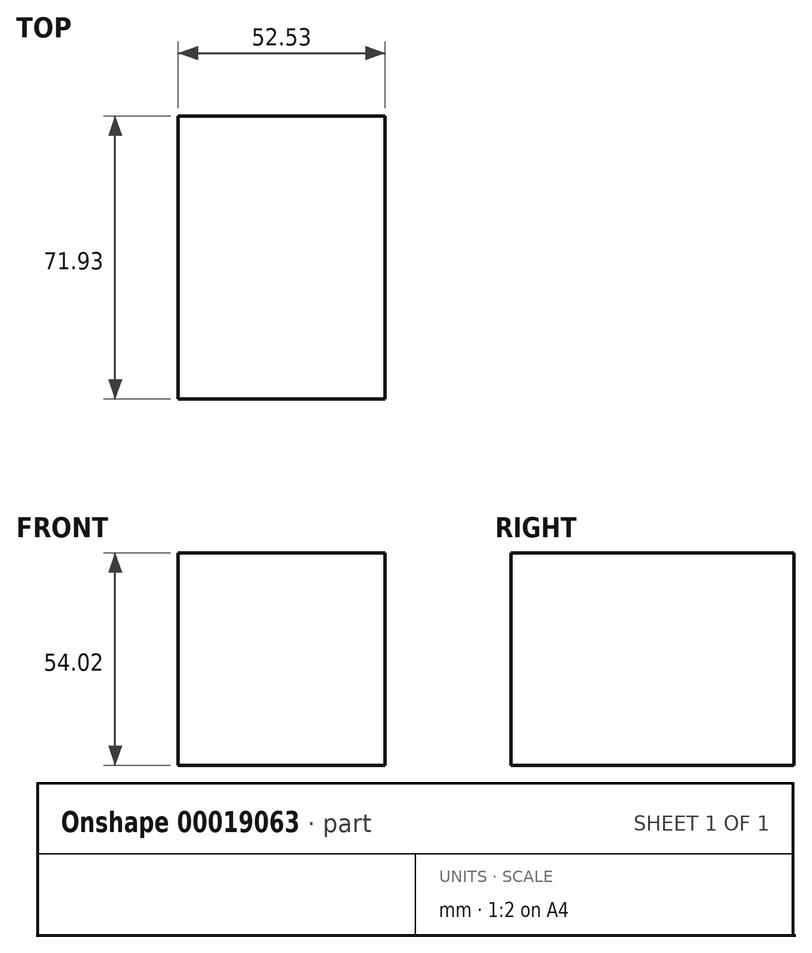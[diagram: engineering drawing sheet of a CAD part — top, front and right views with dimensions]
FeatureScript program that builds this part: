
annotation { "Feature Type Name" : "Feature", "Feature Type Description" : "" }
export const myFeature = defineFeature(function(context is Context, id is Id, definition is map)
    precondition{}
    {
        {
            var Q0;
            Q0=qCreatedBy(makeId("Front.planeOp"),FACE);
            var sketch = newSketch(context, id + "F0", { "sketchPlane" : qUnion([Q0])});
            skLineSegment(sketch, "E0.bottom", {"start": v(0, 0) * mm, "end": v(-52.53, 0) * mm});
            skLineSegment(sketch, "E0.top", {"start": v(0, 54.02) * mm, "end": v(-52.53, 54.02) * mm});
            skLineSegment(sketch, "E0.left", {"start": v(0, 0) * mm, "end": v(0, 54.02) * mm});
            skLineSegment(sketch, "E0.right", {"start": v(-52.53, 0) * mm, "end": v(-52.53, 54.02) * mm});
            skSolve(sketch);
        }
        {
            var Q0;
            Q0 = qSketchRegion(id + "F0", true);
            extrude(context, id + "F1", {"entities" : qUnion([Q0]), "oppositeDirection" : true, "depth" : 71.93 * mm});
        }
        {
            var Q0;
            Q0=makeQuery(id+"F1.opExtrude","SWEPT_FACE",FACE,{"disambiguationData":[OSD([sQuery(id+"F0.wireOp",EDGE,"E0.right")])]});
            var sketch = newSketch(context, id + "F2", { "sketchPlane" : qUnion([Q0])});
            skCircle(sketch, "E1", {"center": v(-38.58, 31.67) * mm, "radius": 13 * mm});
            skSolve(sketch);
        }
        {
            var Q0;
            Q0=sQuery(id+"F2.wireOp",EDGE,"E1");
            extrude(context, id + "F3", {"bodyType" : ToolBodyType.SURFACE, "surfaceEntities" : qUnion([Q0]), "depth" : 76.2 * mm});
        }
    });
